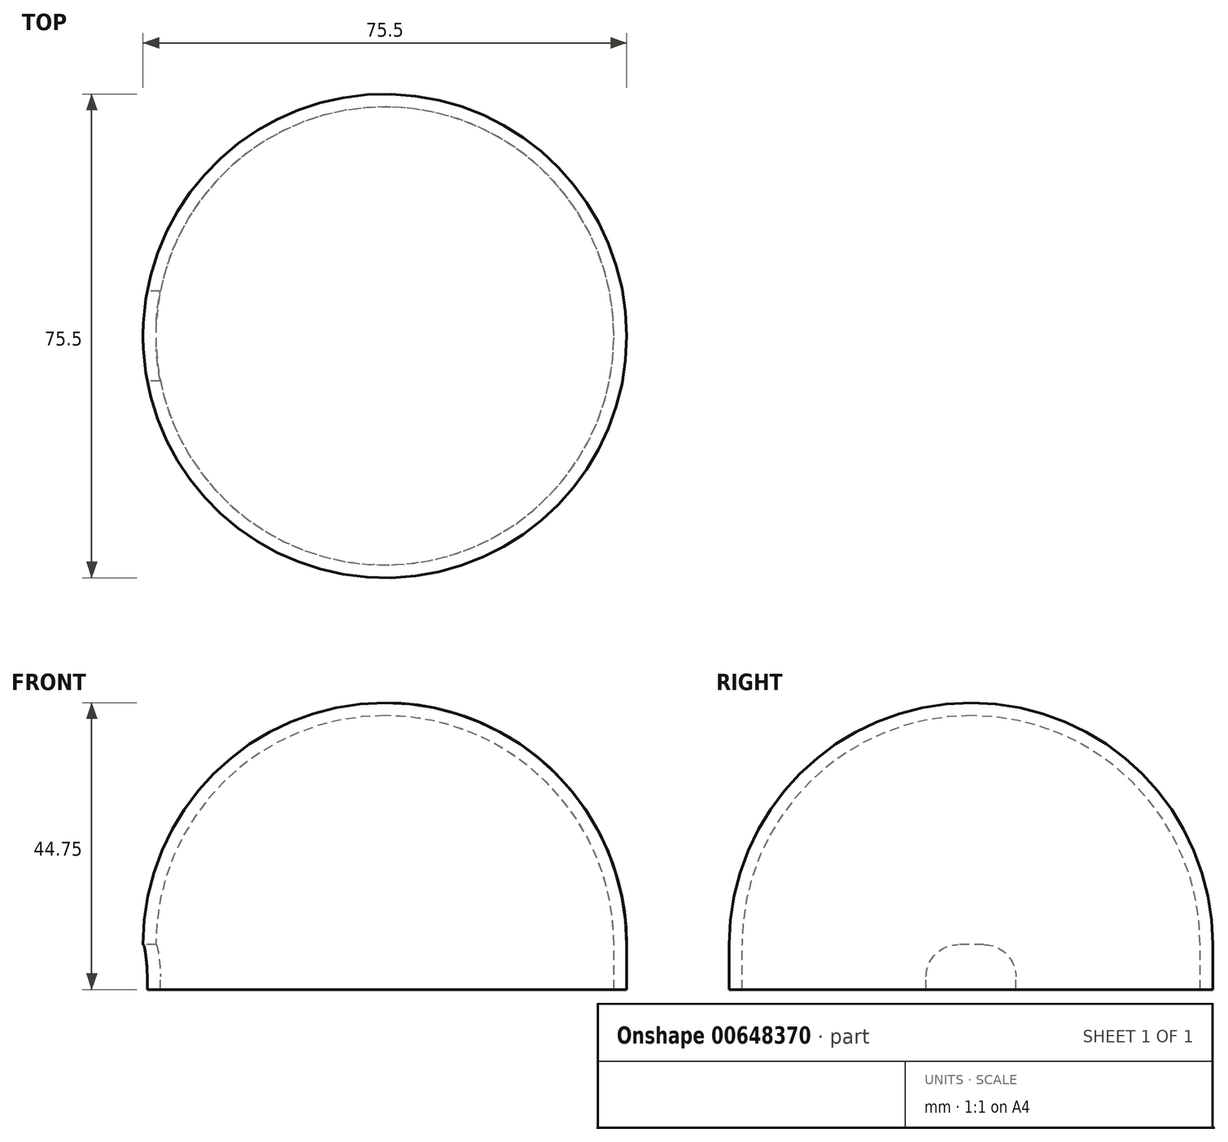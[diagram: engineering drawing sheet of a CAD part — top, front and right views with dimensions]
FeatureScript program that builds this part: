
annotation { "Feature Type Name" : "Feature", "Feature Type Description" : "" }
export const myFeature = defineFeature(function(context is Context, id is Id, definition is map)
    precondition{}
    {
        {
            var Q0;
            Q0=qCreatedBy(makeId("Front.planeOp"),FACE);
            var sketch = newSketch(context, id + "F0", { "sketchPlane" : qUnion([Q0])});
            skLineSegment(sketch, "E0", {"start": v(94.42, 38.36) * mm, "end": v(96.42, 38.36) * mm});
            skLineSegment(sketch, "E1", {"start": v(96.42, 38.36) * mm, "end": v(96.42, 45.36) * mm});
            skLineSegment(sketch, "E2", {"start": v(96.42, 45.36) * mm, "end": v(96.42, 45.36) * mm});
            skPoint(sketch, "E3.visualSharp", {"position": v(96.42, 82.1) * mm});
            skLineSegment(sketch, "E4", {"start": v(94.42, 38.36) * mm, "end": v(94.42, 45.36) * mm});
            skLineSegment(sketch, "E5", {"start": v(94.42, 45.36) * mm, "end": v(94.42, 45.36) * mm});
            skPoint(sketch, "E6.visualSharp", {"position": v(94.42, 81.1) * mm});
            skLineSegment(sketch, "E7", {"start": v(58.67, 81.1) * mm, "end": v(58.67, 81.1) * mm});
            skArc(sketch, "E8.filletArc", {"start": v(94.42, 45.36) * mm, "mid": v(83.95, 70.64) * mm, "end": v(58.67, 81.1) * mm});
            skLineSegment(sketch, "E9", {"start": v(58.67, 81.1) * mm, "end": v(58.67, 83.1) * mm});
            skLineSegment(sketch, "E10", {"start": v(58.67, 83.1) * mm, "end": v(58.67, 83.1) * mm});
            skPoint(sketch, "E11.visualSharp", {"position": v(96.42, 83.1) * mm});
            skArc(sketch, "E11.filletArc", {"start": v(96.42, 45.36) * mm, "mid": v(85.36, 72.05) * mm, "end": v(58.67, 83.1) * mm});
            skLineSegment(sketch, "E12", {"start": v(58.67, 82.1) * mm, "end": v(58.67, 59.86) * mm, "construction": true});
            skSolve(sketch);
        }
        {
            var Q0;
            Q0=makeQuery(id+"F0.imprint","IMPRINT",FACE,{"disambiguationData":[TD([[makeQuery(id+"F0.imprint","IMPRINT",EDGE,{"derivedFrom":sQuery(id+"F0.wireOp",EDGE,"E0")}),1.0]])]});
            var Q1;
            Q1=sQuery(id+"F0.wireOp",EDGE,"E12");
            revolve(context, id + "F1", {"entities" : qUnion([Q0]), "axis" : qUnion([Q1]), "revolveType" : RevolveType.FULL});
        }
        {
            var Q0;
            Q0=qCreatedBy(makeId("Right.planeOp"),FACE);
            var sketch = newSketch(context, id + "F2", { "sketchPlane" : qUnion([Q0])});
            skLineSegment(sketch, "E13.bottom", {"start": v(2, 45.36) * mm, "end": v(-2, 45.36) * mm});
            skLineSegment(sketch, "E13.top", {"start": v(7, 38.36) * mm, "end": v(-7, 38.36) * mm});
            skLineSegment(sketch, "E13.left", {"start": v(7, 40.36) * mm, "end": v(7, 38.36) * mm});
            skLineSegment(sketch, "E13.right", {"start": v(-7, 40.36) * mm, "end": v(-7, 38.36) * mm});
            skPoint(sketch, "E14.visualSharp", {"position": v(7, 45.36) * mm});
            skArc(sketch, "E14.filletArc", {"start": v(7, 40.36) * mm, "mid": v(5.54, 43.9) * mm, "end": v(2, 45.36) * mm});
            skPoint(sketch, "E15.visualSharp", {"position": v(-7, 45.36) * mm});
            skArc(sketch, "E15.filletArc", {"start": v(-2, 45.36) * mm, "mid": v(-5.54, 43.9) * mm, "end": v(-7, 40.36) * mm});
            skSolve(sketch);
        }
        {
            var Q0;
            Q0 = qSketchRegion(id + "F2", true);
            extrude(context, id + "F3", {"entities" : qUnion([Q0]), "operationType" : NewBodyOperationType.REMOVE, "depth" : 25 * mm, "offsetDistance" : 25 * mm});
        }
    });
